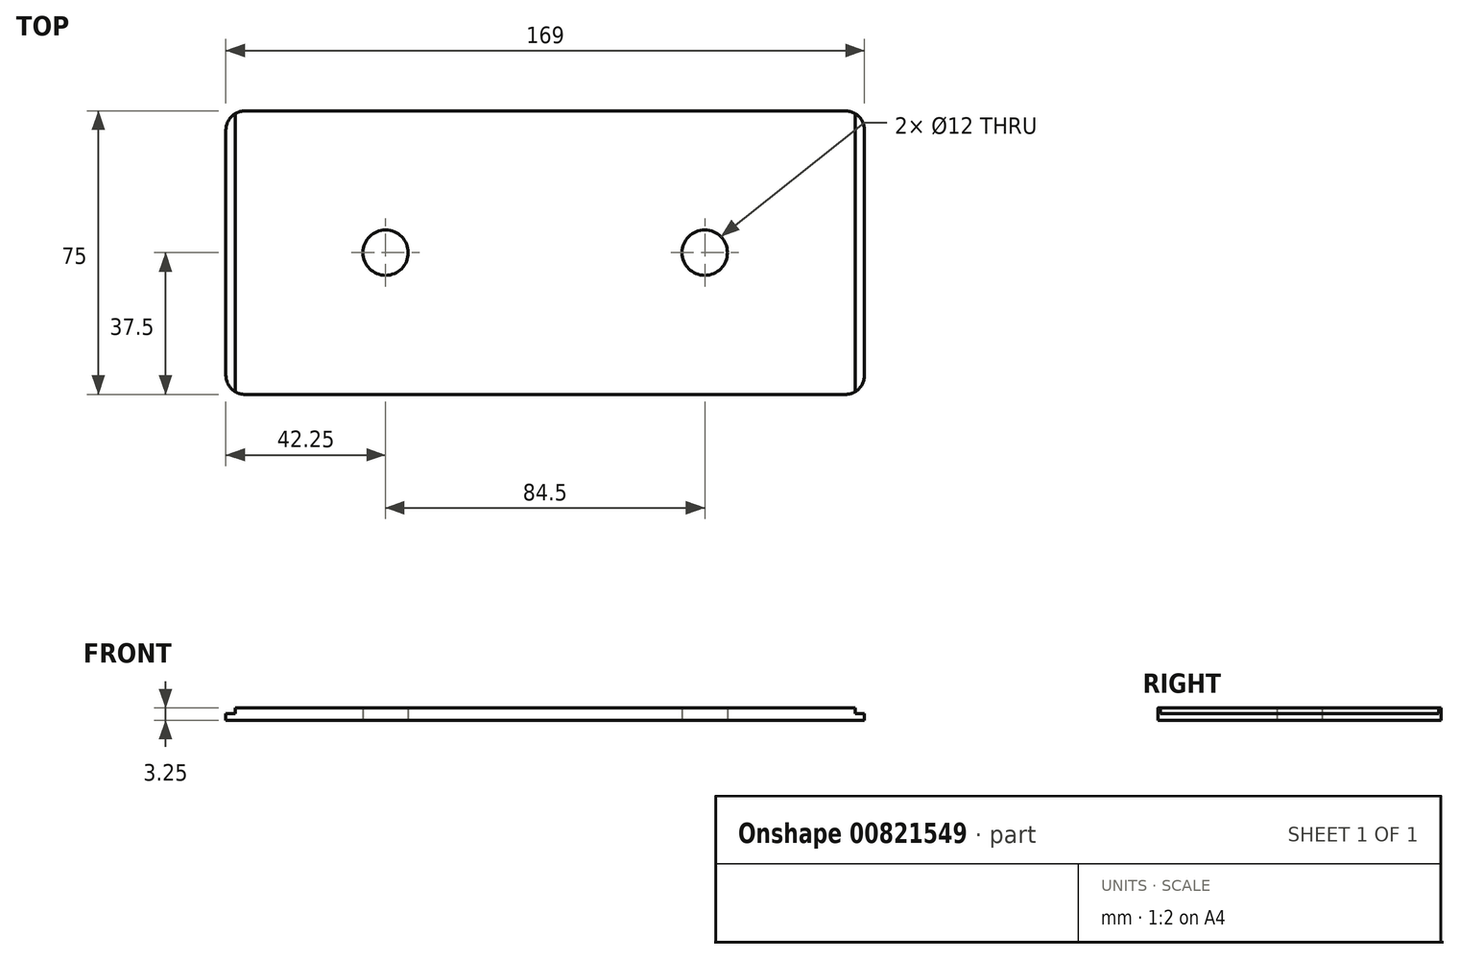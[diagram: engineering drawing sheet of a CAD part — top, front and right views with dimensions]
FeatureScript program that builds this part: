
annotation { "Feature Type Name" : "Feature", "Feature Type Description" : "" }
export const myFeature = defineFeature(function(context is Context, id is Id, definition is map)
    precondition{}
    {
        {
            var Q0;
            Q0=qCreatedBy(makeId("Top.planeOp"),FACE);
            var sketch = newSketch(context, id + "F0", { "sketchPlane" : qUnion([Q0])});
            skLineSegment(sketch, "E0.bottom", {"start": v(84.5, -37.5) * mm, "end": v(-84.5, -37.5) * mm});
            skLineSegment(sketch, "E0.top", {"start": v(84.5, 37.5) * mm, "end": v(-84.5, 37.5) * mm});
            skLineSegment(sketch, "E0.left", {"start": v(84.5, -37.5) * mm, "end": v(84.5, 37.5) * mm});
            skLineSegment(sketch, "E0.right", {"start": v(-84.5, -37.5) * mm, "end": v(-84.5, 37.5) * mm});
            skPoint(sketch, "E0.middle", {"position": v(0, 0) * mm});
            skLineSegment(sketch, "E1", {"start": v(-84.5, 0) * mm, "end": v(0, 0) * mm, "construction": true});
            skCircle(sketch, "E2", {"center": v(-42.25, 0) * mm, "radius": 6 * mm});
            skLineSegment(sketch, "E3", {"start": v(0, 0) * mm, "end": v(84.5, 0) * mm, "construction": true});
            skCircle(sketch, "E4", {"center": v(42.25, 0) * mm, "radius": 6 * mm});
            skSolve(sketch);
        }
        {
            var Q0;
            Q0 = qSketchRegion(id + "F0", true);
            extrude(context, id + "F1", {"entities" : qUnion([Q0]), "depth" : 1.75 * mm, "offsetDistance" : 25 * mm});
        }
        {
            var Q0;
            Q0=makeQuery(id+"F1.opExtrude","CAP_FACE",FACE,{"disambiguationData":[OSD([sQuery(id+"F0.wireOp",EDGE,"E0.bottom"),sQuery(id+"F0.wireOp",EDGE,"E0.top"),sQuery(id+"F0.wireOp",EDGE,"E0.left"),sQuery(id+"F0.wireOp",EDGE,"E0.right"),sQuery(id+"F0.wireOp",EDGE,"E2"),sQuery(id+"F0.wireOp",EDGE,"E4")])],"isStart":false});
            var sketch = newSketch(context, id + "F2", { "sketchPlane" : qUnion([Q0])});
            skLineSegment(sketch, "E5.bottom", {"start": v(-82, 37.5) * mm, "end": v(82, 37.5) * mm});
            skLineSegment(sketch, "E5.top", {"start": v(-82, -37.5) * mm, "end": v(82, -37.5) * mm});
            skLineSegment(sketch, "E5.left", {"start": v(-82, 37.5) * mm, "end": v(-82, -37.5) * mm});
            skLineSegment(sketch, "E5.right", {"start": v(82, 37.5) * mm, "end": v(82, -37.5) * mm});
            skPoint(sketch, "E5.middle", {"position": v(0, 0) * mm});
            skSolve(sketch);
        }
        {
            var Q0;
            Q0 = qSketchRegion(id + "F2", true);
            extrude(context, id + "F3", {"entities" : qUnion([Q0]), "operationType" : NewBodyOperationType.ADD, "depth" : 1.5 * mm, "offsetDistance" : 25 * mm});
        }
        {
            var Q0;
            Q0=makeQuery(id+"F1.opExtrude","SWEPT_EDGE",EDGE,{"disambiguationData":[OSD([sQuery(id+"F0.wireOp",EDGE,"E0.bottom"),sQuery(id+"F0.wireOp",EDGE,"E0.right")])]});
            var Q1;
            Q1=makeQuery(id+"F1.opExtrude","SWEPT_EDGE",EDGE,{"disambiguationData":[OSD([sQuery(id+"F0.wireOp",EDGE,"E0.bottom"),sQuery(id+"F0.wireOp",EDGE,"E0.left")])]});
            var Q2;
            Q2=makeQuery(id+"F1.opExtrude","SWEPT_EDGE",EDGE,{"disambiguationData":[OSD([sQuery(id+"F0.wireOp",EDGE,"E0.top"),sQuery(id+"F0.wireOp",EDGE,"E0.left")])]});
            var Q3;
            Q3=makeQuery(id+"F1.opExtrude","SWEPT_EDGE",EDGE,{"disambiguationData":[OSD([sQuery(id+"F0.wireOp",EDGE,"E0.top"),sQuery(id+"F0.wireOp",EDGE,"E0.right")])]});
            fillet(context, id + "F4", {"entities" : qUnion([Q0, Q1, Q2, Q3]), "radius" : 5 * mm, "tangentPropagation" : true, "allowEdgeOverflow" : false});
        }
        {
            var Q0;
            Q0=makeQuery(id+"F0.imprint","IMPRINT",FACE,{"disambiguationData":[TD([[makeQuery(id+"F0.imprint","IMPRINT",EDGE,{"derivedFrom":sQuery(id+"F0.wireOp",EDGE,"E4")}),1.0]])]});
            var Q1;
            Q1=makeQuery(id+"F0.imprint","IMPRINT",FACE,{"disambiguationData":[TD([[makeQuery(id+"F0.imprint","IMPRINT",EDGE,{"derivedFrom":sQuery(id+"F0.wireOp",EDGE,"E2")}),1.0]])]});
            extrude(context, id + "F5", {"entities" : qUnion([Q0, Q1]), "operationType" : NewBodyOperationType.REMOVE, "depth" : 25 * mm, "offsetDistance" : 25 * mm});
        }
    });
